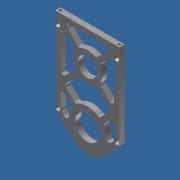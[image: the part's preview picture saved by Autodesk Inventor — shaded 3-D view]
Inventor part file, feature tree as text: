
AUTODESK INVENTOR PART (.ipt)
format: ipt  version: 2012 (Build 160160000, 160)  size: 246,272 bytes
history: native  units: in
note: dims shown in document units (in); Inventor stores cm internally (conversion verified against a paired STEP export)
features: sketch x3, extrude x2, fillet x2, hole x2
ambient origin geometry x8: Origin, YZ Plane, XZ Plane, XY Plane, X Axis, Y Axis, Z Axis, Center Point
bodies: Solid1 (feature_tree)
feature tree (9):
  sketch  "Sketch1"  dims[d0=3.0in d1=1.5in d2=4.0in]
  extrude  "Extrusion1"  Depth=1.5in
  fillet  "Fillet1"  Radius=4.0in
  sketch  "Sketch2"  dims[d3=2.0in d4=4.0in]
  hole  "Hole3"  [1 undecoded]
  hole  "Hole4"  [1 undecoded]
  extrude  "Extrusion4"  Depth=1.125in
  fillet  "Fillet4"  Radius=1.5in
  sketch  "Sketch3"  dims[d5=1.5in d6=1.5in d7=1.125in d8=1.5in d9=1.5in d10=0.875in d11=1.5in d13=0.125in d14=0.5in d15=0.125in d16=0.125in d17=0.125in d18=0.125in d21=0.25in d22=0.0in d23=1.061in d31=0.125in d32=0.5in d70=0.125in d71=0.75in d72=0.25in d73=0.25in d74=0.5635in d75=1.0in d76=0.8108in d77=0.125in d78=0.125in d79=0.125in d80=0.125in d81=0.75in d82=0.25in d83=0.25in d84=0.5635in d85=0.375in d86=0.8108in d88=2.4606in d92=0.5in d93=0.125in d94=0.7874in d96=3.375in d97=0.7874in d99=2.75in d106=0.25in d107=0.25in d108=0.25in d109=0.25in d110=0.25in d111=0.875in d112=0.6875in d113=0.25in d114=0.125in d115=0.25in d116=0.125in d117=0.25in d118=0.125in d119=0.25in d120=0.125in d121=0.25in d122=0.25in d123=1.0in d124=0.0in d125=0.125in]
note: 2 required parameter values undecoded (feature->parameter linkage not recoverable at this tier; creation-order binding heuristic only, values carry confidence <= 0.55)
